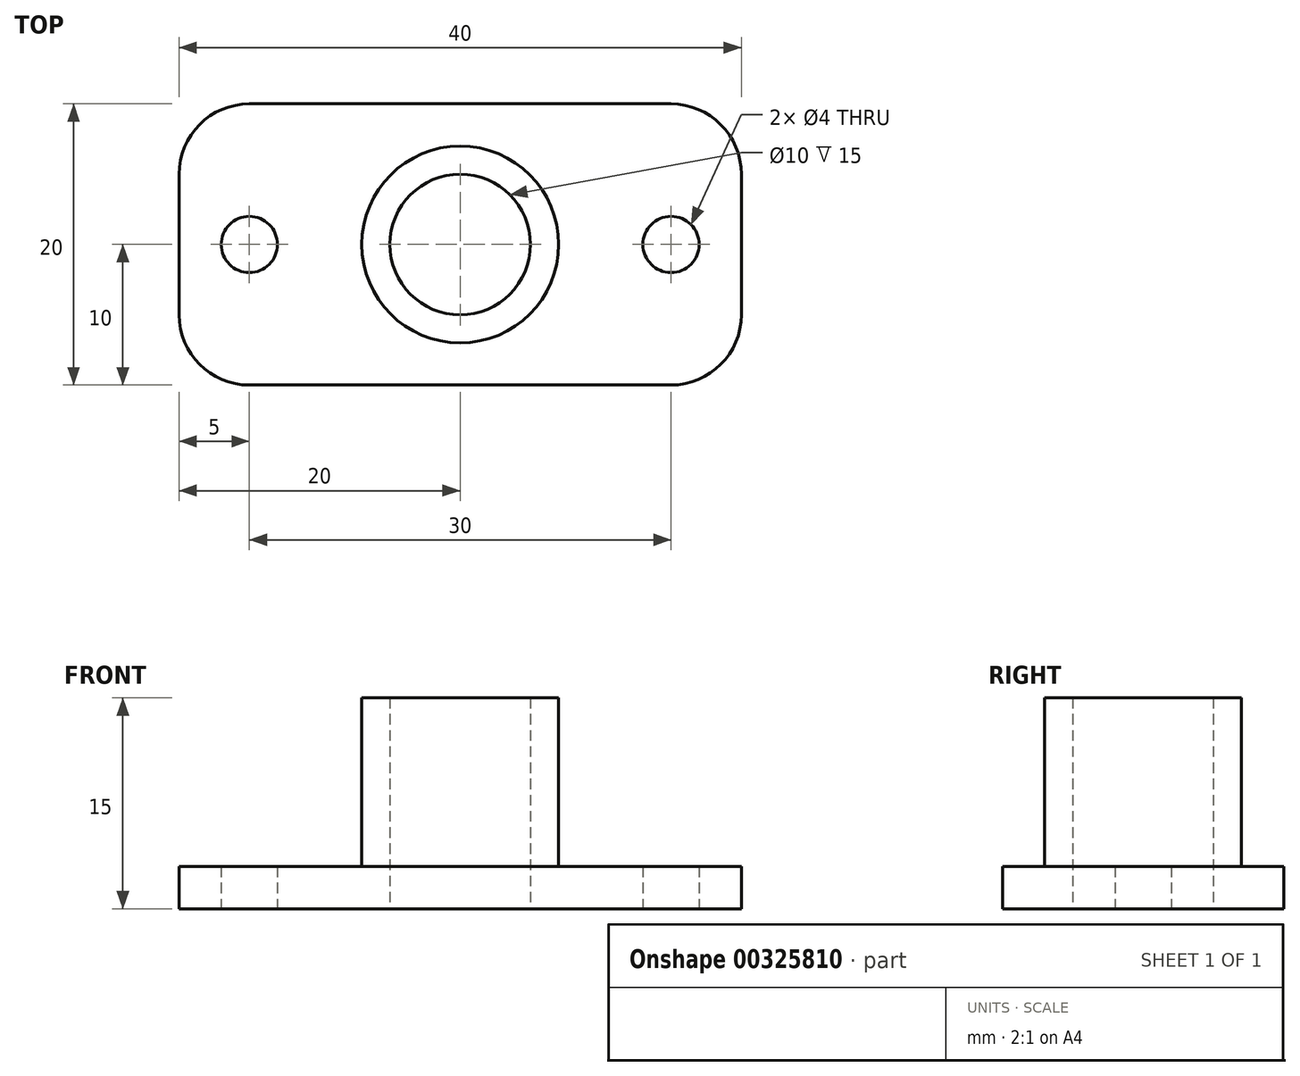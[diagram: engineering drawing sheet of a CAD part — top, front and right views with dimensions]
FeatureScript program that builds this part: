
annotation { "Feature Type Name" : "Feature", "Feature Type Description" : "" }
export const myFeature = defineFeature(function(context is Context, id is Id, definition is map)
    precondition{}
    {
        {
            var Q0;
            Q0=qCreatedBy(makeId("Top.planeOp"),FACE);
            var sketch = newSketch(context, id + "F0", { "sketchPlane" : qUnion([Q0])});
            skLineSegment(sketch, "E0.bottom", {"start": v(20, 10) * mm, "end": v(-20, 10) * mm});
            skLineSegment(sketch, "E0.top", {"start": v(20, -10) * mm, "end": v(-20, -10) * mm});
            skLineSegment(sketch, "E0.left", {"start": v(20, 10) * mm, "end": v(20, -10) * mm});
            skLineSegment(sketch, "E0.right", {"start": v(-20, 10) * mm, "end": v(-20, -10) * mm});
            skPoint(sketch, "E0.middle", {"position": v(0, 0) * mm});
            skCircle(sketch, "E1", {"center": v(0, 0) * mm, "radius": 5 * mm});
            skCircle(sketch, "E2", {"center": v(-15, 0) * mm, "radius": 2 * mm});
            skCircle(sketch, "E3", {"center": v(0, 0) * mm, "radius": 7 * mm});
            skCircle(sketch, "E4.MirrorC", {"center": v(15, 0) * mm, "radius": 2 * mm});
            skSolve(sketch);
        }
        {
            var Q0;
            Q0=makeQuery(id+"F0.imprint","IMPRINT",FACE,{"disambiguationData":[TD([[makeQuery(id+"F0.imprint","IMPRINT",EDGE,{"derivedFrom":sQuery(id+"F0.wireOp",EDGE,"E0.bottom")}),1.0]])]});
            var Q1;
            Q1=makeQuery(id+"F0.imprint","IMPRINT",FACE,{"disambiguationData":[TD([[makeQuery(id+"F0.imprint","IMPRINT",EDGE,{"derivedFrom":sQuery(id+"F0.wireOp",EDGE,"E1")}),-1.0]])]});
            extrude(context, id + "F1", {"entities" : qUnion([Q0, Q1]), "depth" : 3 * mm});
        }
        {
            var Q0;
            Q0=makeQuery(id+"F0.imprint","IMPRINT",FACE,{"disambiguationData":[TD([[makeQuery(id+"F0.imprint","IMPRINT",EDGE,{"derivedFrom":sQuery(id+"F0.wireOp",EDGE,"E1")}),-1.0]])]});
            extrude(context, id + "F2", {"entities" : qUnion([Q0]), "operationType" : NewBodyOperationType.ADD, "depth" : 15 * mm});
        }
        {
            var Q0;
            Q0=makeQuery(id+"F1.opExtrude","SWEPT_EDGE",EDGE,{"disambiguationData":[OSD([sQuery(id+"F0.wireOp",EDGE,"E0.bottom"),sQuery(id+"F0.wireOp",EDGE,"E0.right")])]});
            var Q1;
            Q1=makeQuery(id+"F1.opExtrude","SWEPT_EDGE",EDGE,{"disambiguationData":[OSD([sQuery(id+"F0.wireOp",EDGE,"E0.top"),sQuery(id+"F0.wireOp",EDGE,"E0.right")])]});
            var Q2;
            Q2=makeQuery(id+"F1.opExtrude","SWEPT_EDGE",EDGE,{"disambiguationData":[OSD([sQuery(id+"F0.wireOp",EDGE,"E0.top"),sQuery(id+"F0.wireOp",EDGE,"E0.left")])]});
            var Q3;
            Q3=makeQuery(id+"F1.opExtrude","SWEPT_EDGE",EDGE,{"disambiguationData":[OSD([sQuery(id+"F0.wireOp",EDGE,"E0.bottom"),sQuery(id+"F0.wireOp",EDGE,"E0.left")])]});
            fillet(context, id + "F3", {"entities" : qUnion([Q0, Q1, Q2, Q3]), "radius" : 5 * mm, "tangentPropagation" : true, "allowEdgeOverflow" : false});
        }
    });
